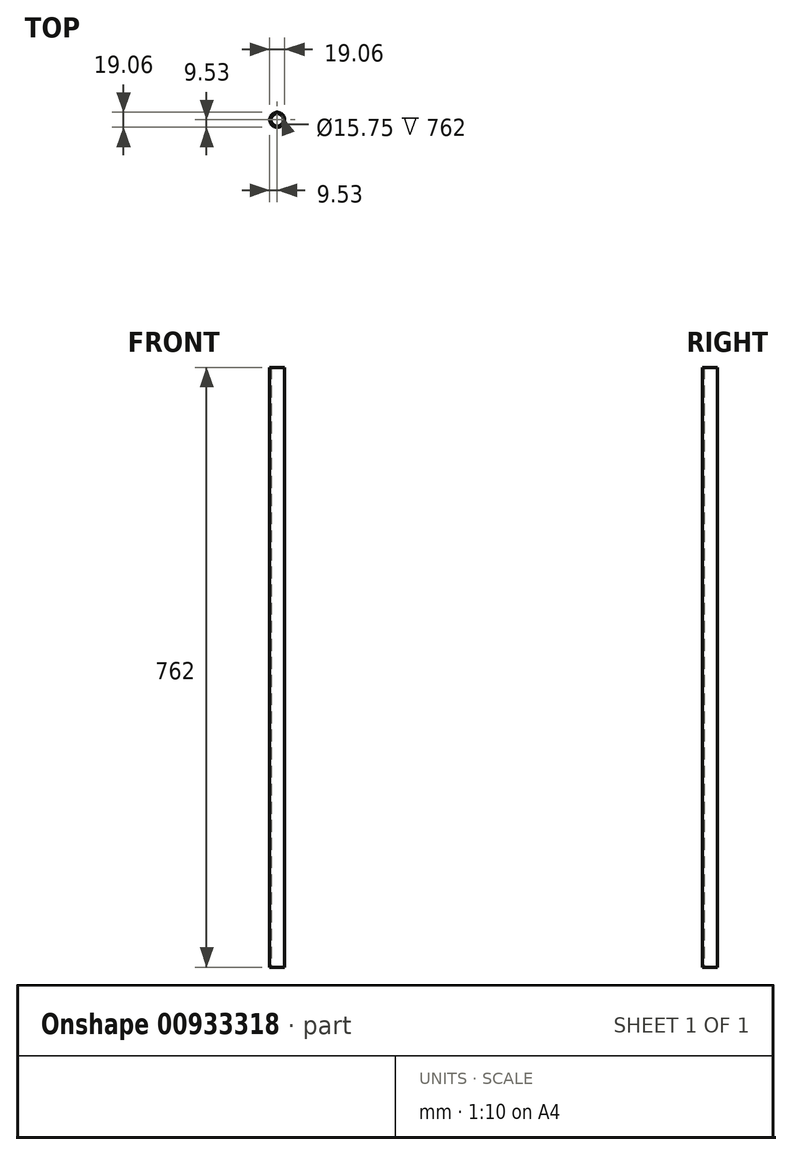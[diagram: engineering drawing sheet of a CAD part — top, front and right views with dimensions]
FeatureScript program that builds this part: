
annotation { "Feature Type Name" : "Feature", "Feature Type Description" : "" }
export const myFeature = defineFeature(function(context is Context, id is Id, definition is map)
    precondition{}
    {
        {
            var Q0;
            Q0=qCreatedBy(makeId("Top.planeOp"),FACE);
            var sketch = newSketch(context, id + "F0", { "sketchPlane" : qUnion([Q0])});
            skCircle(sketch, "E0", {"center": v(0, 0) * mm, "radius": 9.53 * mm});
            skCircle(sketch, "E1", {"center": v(0, 0) * mm, "radius": 7.87 * mm});
            skSolve(sketch);
        }
        {
            var Q0;
            Q0=makeQuery(id+"F0.imprint","IMPRINT",FACE,{"disambiguationData":[TD([[makeQuery(id+"F0.imprint","IMPRINT",EDGE,{"derivedFrom":sQuery(id+"F0.wireOp",EDGE,"E0")}),1.0]])]});
            extrude(context, id + "F1", {"entities" : qUnion([Q0]), "depth" : 762 * mm, "offsetDistance" : 25.4 * mm});
        }
    });
